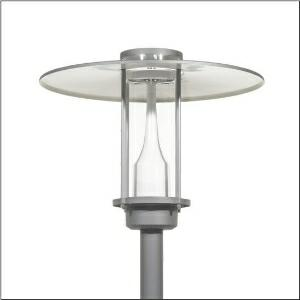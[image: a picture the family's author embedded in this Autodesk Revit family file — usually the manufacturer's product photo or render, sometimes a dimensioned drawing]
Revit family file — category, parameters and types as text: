
# Revit family: city-light_plus_iq___p1_0a_5xa5275ff14hp_3a67
name_source: partatom
category: Lighting Fixtures
units: mm (PartAtom-declared; Revit-internal decimal feet)

## family parameters
Cut with Voids When Loaded = No
Host = Face
Light Source = No
Part Type = Normal
Room Calculation Point = No
Round Connector Dimension = Use Diameter
Shared = No

## types (1)
- --- (1 x LED, 4480 lm, 33.6 W, 3000K)
    Apparent Load = 34 VA
    CIE Flux Codes = 30 60 90 96 100
    Color Rendering = 70
    Color Temperature = 3000K
    Default Elevation = 1800 mm
    Description = City-Light Plus iQ, mast luminaire, Module 540 iQ-SR, primary light control with 3 zone facetted reflector, of plastic, silver coated, highly specular, structured, primary optical cover: cover, of PMMA, transparent, light distribution: P1.0a, light emission: direct distribution, primary light characteristic: strongly asymmetric, installation type: post-top, LED, High Power LED, rated luminous flux: 4.480lm, luminous efficacy: 133lm/W, light colour: 730, colour temperature: 3000K, control gear: iQ Street-Remote, control: pre-setting: logarithmic dimming characteristic, Street-Remote, Auto-Match, Temp-Guard, Lumen-Switch, Night-Set, Smart-Wire, Light-Fading, Desk-Remote (wireless, voltage-free reading and setting of iQ features in the workshop via application-optimized NFC function/RFID function), optimised constant luminous flux control (CLO 2.0), with terminal, 6-pole, max. 2.5mm², mains connection: 230..240V, AC, 50/60Hz, start of lifetime: 34W, end of service life: 36W, reduction: 15W, luminaire housing, upper part, of glass-fibre reinforced polyester, coated, Siteco® metallic grey (DB 702S), diameter: 750mm, height: 590mm, spigot size: d x l = 76 x 70mm (post-top) | with reducer (optional accessory) 60 x 70mm, mounting height: 3..5m, post-top mast mounting element, of diecast aluminium, coated, Siteco® metallic grey (DB 702S), Module 540 iQ-SR, traffic white (RAL 9016), equipment: Power, protection rating (complete): IP65, insulation class (complete): insulation class II (safety insulation), certification: CE, ENEC, VDE, packaging unit: 1 piece

Light Distribution: P1.0a
    Height = 590 mm
    Lamp = 1 x LED
    Lamp Light Flux = 4480 lm
    Lamp Power = 33.6 W
    Lamp count = 1
    Length = 750 mm
    Luminous efficacy = 133 lm/W
    Manufacturer = Siteco
    ModVariant = No
    Model = 5XA5275FF14HP
    Number of Poles = 1
    OnlyDefault = Yes
    Power Factor = 1
    Product Name = City-Light Plus iQ | P1.0a
    Product group = mast luminaire | pylon top
    ProductGroupID = 6100
    Protection Class = Protection class II
    Protection Degree = IP 65
    RLX_Detail_Level = 1
    RLX_Emergency_Light_Flux = 0 lm
    RLX_Emergency_Type = 0
    RLX_Emergency_Type_DB = No
    RlxData = <blob elided: 52733 chars, md5=b7818f7c>
    Socket = socket
    Standby Power = 0 W
    System Light Flux = 4480 lm
    System Power = 34 W
    Type Comments = factory setting: luminous flux: 100 % | dim-lin: 254 | 695 mA
    Type Image = l_1006456.jpg
    URL = http://relux.com
    VarID = @adj_191199
    Voltage = 0 V
    Weight = 0.00 kg
    Width = 0 mm  [stored 0 ft]

note: [stored X ft] marks values corroborated as IEEE doubles in the binary element streams (Revit-internal decimal feet)

## geometry (parser evidence)
native form markers: Blend x4, Sweep x12
no freeform markers — native parametric forms only
